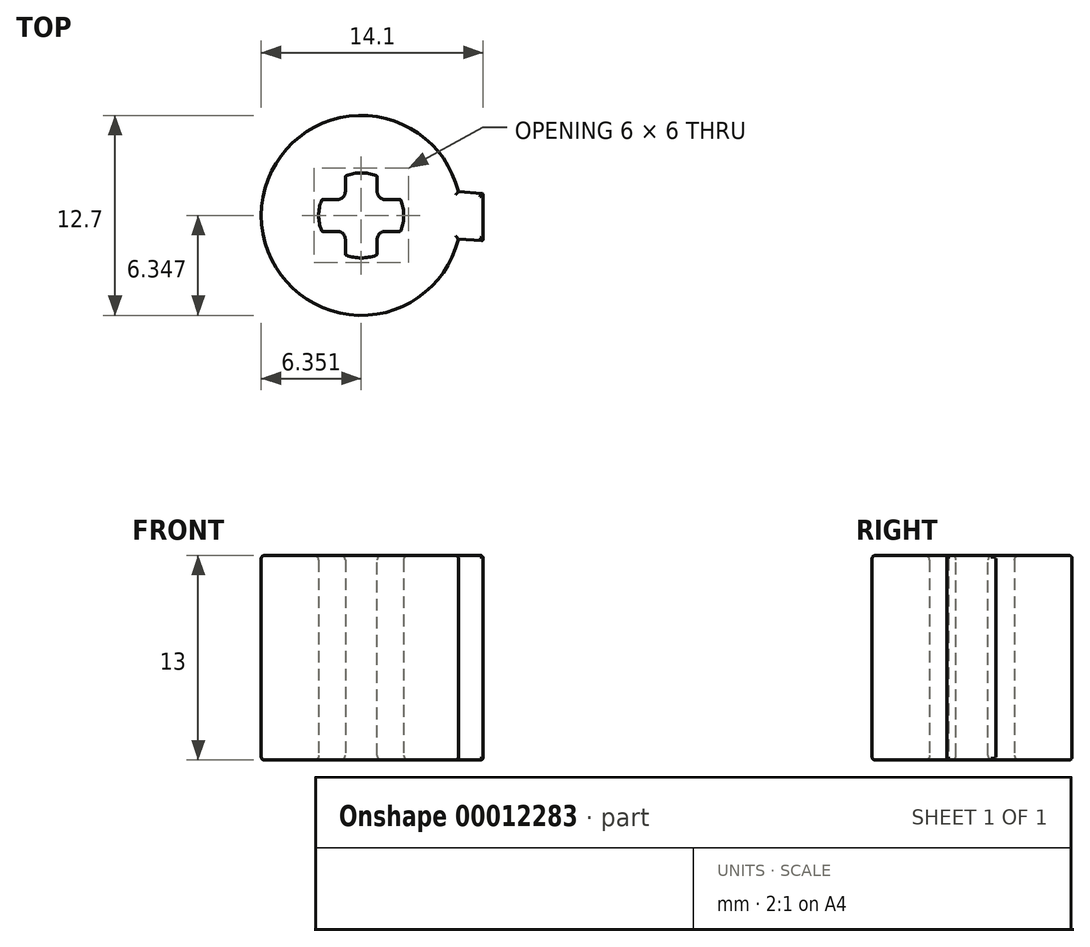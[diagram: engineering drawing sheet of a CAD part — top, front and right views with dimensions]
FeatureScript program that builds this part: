
annotation { "Feature Type Name" : "Feature", "Feature Type Description" : "" }
export const myFeature = defineFeature(function(context is Context, id is Id, definition is map)
    precondition{}
    {
        {
            var Q0;
            Q0=qCreatedBy(makeId("Top.planeOp"),FACE);
            var sketch = newSketch(context, id + "F0", { "sketchPlane" : qUnion([Q0])});
            skLineSegment(sketch, "E0.right", {"start": v(14, 0) * mm, "end": v(14, -3) * mm});
            skArc(sketch, "E1", {"start": v(12.42, 0.12) * mm, "mid": v(-0.1, -1.4) * mm, "end": v(12.42, -2.9) * mm});
            skLineSegment(sketch, "E2.trimOffspring", {"start": v(12.42, 0.12) * mm, "end": v(14, 0) * mm});
            skLineSegment(sketch, "E3.trimOffspring", {"start": v(12.42, -2.9) * mm, "end": v(14, -3) * mm});
            skArc(sketch, "E4", {"start": v(7.26, 1.11) * mm, "mid": v(6.25, 1.3) * mm, "end": v(5.24, 1.11) * mm});
            skLineSegment(sketch, "E5", {"start": v(5.24, -0.38) * mm, "end": v(5.24, 1.11) * mm});
            skLineSegment(sketch, "E6", {"start": v(7.26, -0.38) * mm, "end": v(7.26, 1.11) * mm});
            skLineSegment(sketch, "E7", {"start": v(7.26, -2.4) * mm, "end": v(7.26, -3.9) * mm});
            skLineSegment(sketch, "E8", {"start": v(5.24, -2.4) * mm, "end": v(5.24, -3.9) * mm});
            skLineSegment(sketch, "E9", {"start": v(7.26, -0.38) * mm, "end": v(8.75, -0.38) * mm});
            skLineSegment(sketch, "E10", {"start": v(5.24, -0.38) * mm, "end": v(3.75, -0.38) * mm});
            skLineSegment(sketch, "E11", {"start": v(5.24, -2.4) * mm, "end": v(3.75, -2.4) * mm});
            skLineSegment(sketch, "E12", {"start": v(7.26, -2.4) * mm, "end": v(8.75, -2.4) * mm});
            skArc(sketch, "E13.trimOffspring", {"start": v(3.75, -0.38) * mm, "mid": v(3.55, -1.4) * mm, "end": v(3.75, -2.4) * mm});
            skArc(sketch, "E14.trimOffspring", {"start": v(5.24, -3.9) * mm, "mid": v(6.25, -4.1) * mm, "end": v(7.26, -3.9) * mm});
            skArc(sketch, "E15.trimOffspring", {"start": v(8.75, -2.4) * mm, "mid": v(8.95, -1.4) * mm, "end": v(8.75, -0.38) * mm});
            skSolve(sketch);
        }
        {
            var Q0;
            Q0=makeQuery(id+"F0.imprint","IMPRINT",FACE,{"disambiguationData":[TD([[makeQuery(id+"F0.imprint","IMPRINT",EDGE,{"derivedFrom":sQuery(id+"F0.wireOp",EDGE,"E0.right")}),-1.0]])]});
            extrude(context, id + "F1", {"entities" : qUnion([Q0]), "depth" : 13 * mm});
        }
        {
            var Q0;
            Q0=makeQuery(id+"F1.opExtrude","SWEPT_EDGE",EDGE,{"disambiguationData":[OSD([sQuery(id+"F0.wireOp",EDGE,"E5"),sQuery(id+"F0.wireOp",EDGE,"E10")])]});
            var Q1;
            Q1=makeQuery(id+"F1.opExtrude","SWEPT_EDGE",EDGE,{"disambiguationData":[OSD([sQuery(id+"F0.wireOp",EDGE,"E8"),sQuery(id+"F0.wireOp",EDGE,"E11")])]});
            var Q2;
            Q2=makeQuery(id+"F1.opExtrude","SWEPT_EDGE",EDGE,{"disambiguationData":[OSD([sQuery(id+"F0.wireOp",EDGE,"E6"),sQuery(id+"F0.wireOp",EDGE,"E9")])]});
            var Q3;
            Q3=makeQuery(id+"F1.opExtrude","SWEPT_EDGE",EDGE,{"disambiguationData":[OSD([sQuery(id+"F0.wireOp",EDGE,"E7"),sQuery(id+"F0.wireOp",EDGE,"E12")])]});
            fillet(context, id + "F2", {"entities" : qUnion([Q0, Q1, Q2, Q3]), "radius" : .5 * mm, "tangentPropagation" : true, "allowEdgeOverflow" : false});
        }
        {
            var Q0;
            Q0=makeQuery(id+"F1.opExtrude","SWEPT_EDGE",EDGE,{"disambiguationData":[OSD([sQuery(id+"F0.wireOp",EDGE,"E11"),sQuery(id+"F0.wireOp",EDGE,"E13.trimOffspring")])]});
            var Q1;
            Q1=makeQuery(id+"F1.opExtrude","SWEPT_EDGE",EDGE,{"disambiguationData":[OSD([sQuery(id+"F0.wireOp",EDGE,"E8"),sQuery(id+"F0.wireOp",EDGE,"E14.trimOffspring")])]});
            var Q2;
            Q2=makeQuery(id+"F1.opExtrude","SWEPT_EDGE",EDGE,{"disambiguationData":[OSD([sQuery(id+"F0.wireOp",EDGE,"E7"),sQuery(id+"F0.wireOp",EDGE,"E14.trimOffspring")])]});
            var Q3;
            Q3=makeQuery(id+"F1.opExtrude","SWEPT_EDGE",EDGE,{"disambiguationData":[OSD([sQuery(id+"F0.wireOp",EDGE,"E12"),sQuery(id+"F0.wireOp",EDGE,"E15.trimOffspring")])]});
            var Q4;
            Q4=makeQuery(id+"F1.opExtrude","SWEPT_EDGE",EDGE,{"disambiguationData":[OSD([sQuery(id+"F0.wireOp",EDGE,"E10"),sQuery(id+"F0.wireOp",EDGE,"E13.trimOffspring")])]});
            var Q5;
            Q5=makeQuery(id+"F1.opExtrude","SWEPT_EDGE",EDGE,{"disambiguationData":[OSD([sQuery(id+"F0.wireOp",EDGE,"E4"),sQuery(id+"F0.wireOp",EDGE,"E5")])]});
            var Q6;
            Q6=makeQuery(id+"F1.opExtrude","SWEPT_EDGE",EDGE,{"disambiguationData":[OSD([sQuery(id+"F0.wireOp",EDGE,"E4"),sQuery(id+"F0.wireOp",EDGE,"E6")])]});
            var Q7;
            Q7=makeQuery(id+"F1.opExtrude","SWEPT_EDGE",EDGE,{"disambiguationData":[OSD([sQuery(id+"F0.wireOp",EDGE,"E9"),sQuery(id+"F0.wireOp",EDGE,"E15.trimOffspring")])]});
            fillet(context, id + "F3", {"entities" : qUnion([Q0, Q1, Q2, Q3, Q4, Q5, Q6, Q7]), "radius" : .1 * mm, "tangentPropagation" : true, "allowEdgeOverflow" : false});
        }
        {
            var Q0;
            Q0=makeQuery(id+"F1.opExtrude","CAP_EDGE",EDGE,{"disambiguationData":[OSD([sQuery(id+"F0.wireOp",EDGE,"E4")])],"isStart":false});
            fillet(context, id + "F4", {"entities" : qUnion([Q0]), "radius" : .3 * mm, "tangentPropagation" : true, "allowEdgeOverflow" : false});
        }
        {
            var Q0;
            Q0=makeQuery(id+"F1.opExtrude","CAP_EDGE",EDGE,{"disambiguationData":[OSD([sQuery(id+"F0.wireOp",EDGE,"E4")])],"isStart":true});
            fillet(context, id + "F5", {"entities" : qUnion([Q0]), "radius" : .3 * mm, "tangentPropagation" : true, "allowEdgeOverflow" : false});
        }
        {
            var Q0;
            Q0=makeQuery(id+"F1.opExtrude","CAP_EDGE",EDGE,{"disambiguationData":[OSD([sQuery(id+"F0.wireOp",EDGE,"E1")])],"isStart":false});
            var Q1;
            Q1=makeQuery(id+"F1.opExtrude","CAP_EDGE",EDGE,{"disambiguationData":[OSD([sQuery(id+"F0.wireOp",EDGE,"E3.trimOffspring")])],"isStart":false});
            var Q2;
            Q2=makeQuery(id+"F1.opExtrude","CAP_EDGE",EDGE,{"disambiguationData":[OSD([sQuery(id+"F0.wireOp",EDGE,"E0.right")])],"isStart":false});
            var Q3;
            Q3=makeQuery(id+"F1.opExtrude","CAP_EDGE",EDGE,{"disambiguationData":[OSD([sQuery(id+"F0.wireOp",EDGE,"E2.trimOffspring")])],"isStart":false});
            var Q4;
            Q4=makeQuery(id+"F1.opExtrude","CAP_EDGE",EDGE,{"disambiguationData":[OSD([sQuery(id+"F0.wireOp",EDGE,"E1")])],"isStart":true});
            var Q5;
            Q5=makeQuery(id+"F1.opExtrude","CAP_EDGE",EDGE,{"disambiguationData":[OSD([sQuery(id+"F0.wireOp",EDGE,"E3.trimOffspring")])],"isStart":true});
            var Q6;
            Q6=makeQuery(id+"F1.opExtrude","CAP_EDGE",EDGE,{"disambiguationData":[OSD([sQuery(id+"F0.wireOp",EDGE,"E0.right")])],"isStart":true});
            var Q7;
            Q7=makeQuery(id+"F1.opExtrude","CAP_EDGE",EDGE,{"disambiguationData":[OSD([sQuery(id+"F0.wireOp",EDGE,"E2.trimOffspring")])],"isStart":true});
            fillet(context, id + "F6", {"entities" : qUnion([Q0, Q1, Q2, Q3, Q4, Q5, Q6, Q7]), "radius" : .2 * mm, "tangentPropagation" : true, "allowEdgeOverflow" : false});
        }
        {
            var Q0;
            Q0=makeQuery(id+"F1.opExtrude","SWEPT_EDGE",EDGE,{"disambiguationData":[OSD([sQuery(id+"F0.wireOp",EDGE,"E0.right"),sQuery(id+"F0.wireOp",EDGE,"E3.trimOffspring")])]});
            var Q1;
            Q1=makeQuery(id+"F1.opExtrude","SWEPT_EDGE",EDGE,{"disambiguationData":[OSD([sQuery(id+"F0.wireOp",EDGE,"E0.right"),sQuery(id+"F0.wireOp",EDGE,"E2.trimOffspring")])]});
            fillet(context, id + "F7", {"entities" : qUnion([Q0, Q1]), "radius" : .1 * mm, "tangentPropagation" : true, "allowEdgeOverflow" : false});
        }
    });
